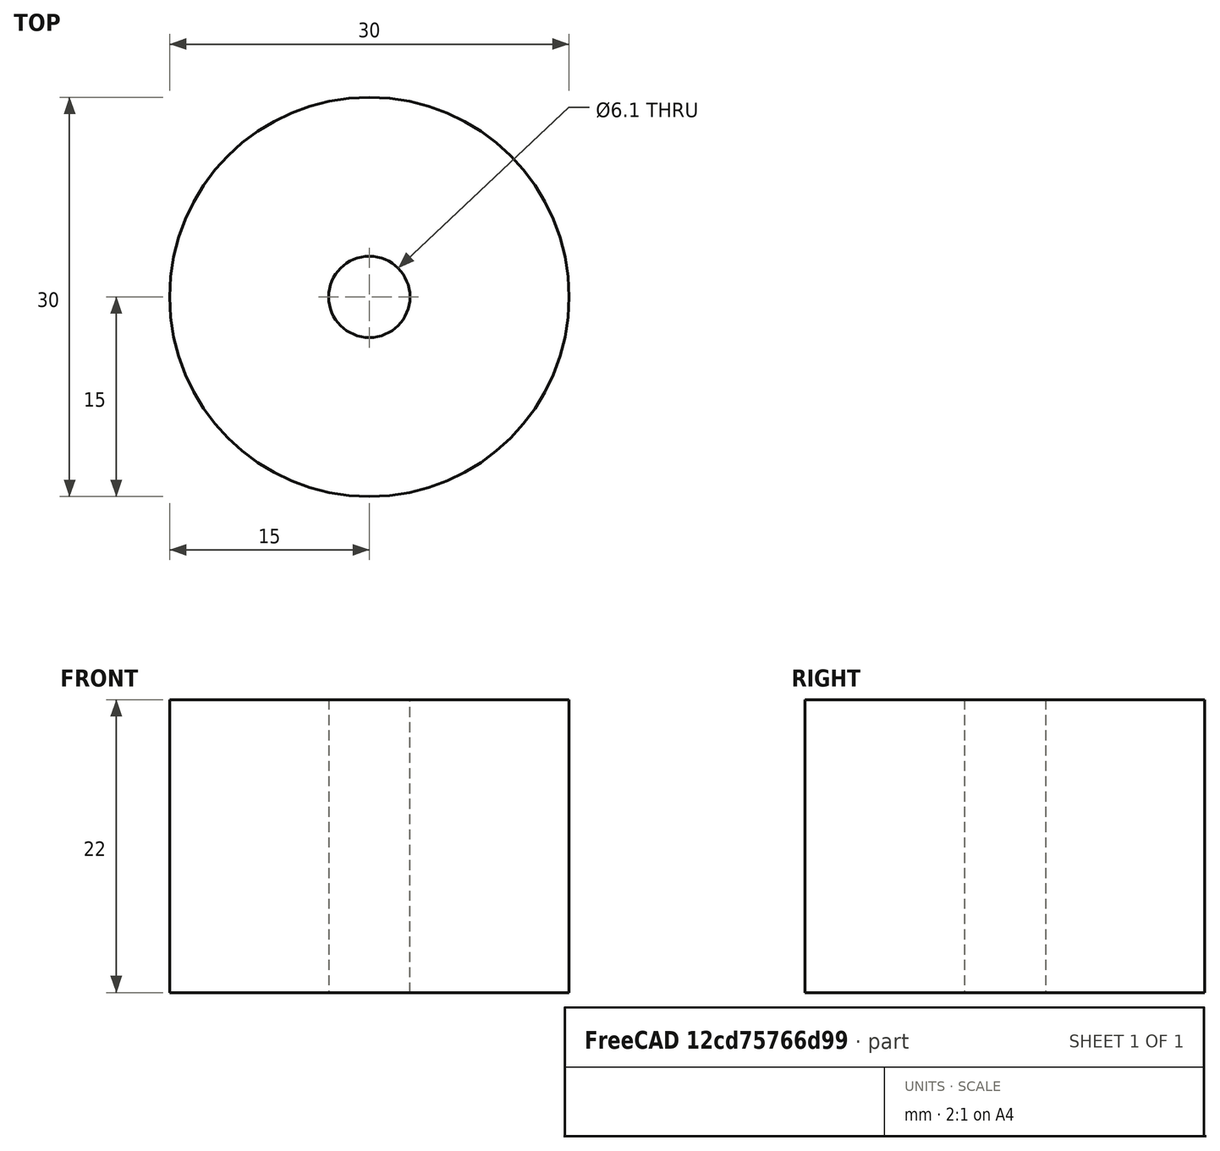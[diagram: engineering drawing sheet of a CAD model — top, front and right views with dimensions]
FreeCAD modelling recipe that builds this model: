
FCSTD DOCUMENT  (FreeCAD 0.19R24291 (Git))
Label: Spacer
License: All rights reserved
LicenseURL: http://en.wikipedia.org/wiki/All_rights_reserved
objects: Sketcher::SketchObject×1, PartDesign::Pad×1, PartDesign::Body×1
note: 4 computed .brp shape members not serialized (recipe doc carries the construction recipe); baked Part::Feature solids carry a one-line shape summary decoded from their .brp

FEATURE [Sketcher::SketchObject] Sketch
  FullyConstrained = true
  MapMode = 5
  Support = -> [XY_Plane]
  sketch-geometry (2):
    g0: Circle CenterX=0 CenterY=0 CenterZ=0 NormalX=0 NormalY=0 NormalZ=1 AngleXU=0 Radius=3.05
    g1: Circle CenterX=0 CenterY=0 CenterZ=0 NormalX=0 NormalY=0 NormalZ=1 AngleXU=0 Radius=15
  constraints (4):
    c: Coincident(g0,g-1)
    c: Coincident(g1,g0)
    c: Diameter(g0) = 6.1
    c: Diameter(g1) = 30
FEATURE [PartDesign::Pad] Pad
  Direction = (1,1,1)
  Length = 22
  Length2 = 100
  Profile = -> Sketch
  Type = 0
FEATURE [PartDesign::Body] Body
  Group = -> [Sketch,Pad]
  Origin = -> Origin
  Tip = -> Pad
